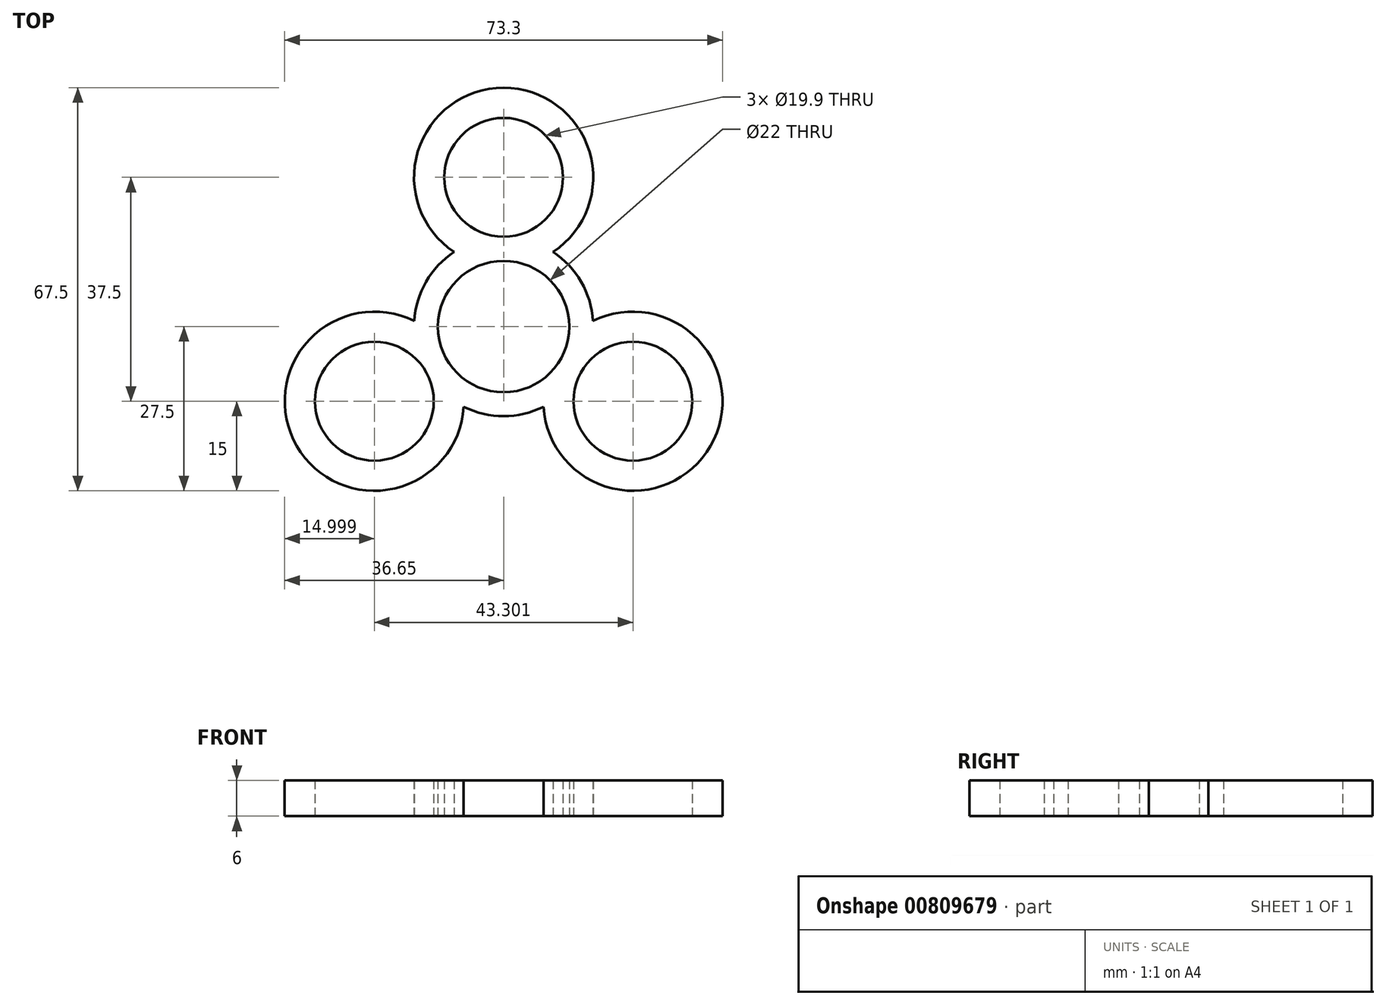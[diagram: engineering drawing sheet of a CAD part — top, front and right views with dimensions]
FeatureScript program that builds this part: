
annotation { "Feature Type Name" : "Feature", "Feature Type Description" : "" }
export const myFeature = defineFeature(function(context is Context, id is Id, definition is map)
    precondition{}
    {
        {
            var Q0;
            Q0=qCreatedBy(makeId("Top.planeOp"),FACE);
            var sketch = newSketch(context, id + "F0", { "sketchPlane" : qUnion([Q0])});
            skArc(sketch, "E0", {"start": v(9.53, 5.5) * mm, "mid": v(0, 11) * mm, "end": v(-9.53, 5.5) * mm});
            skLineSegment(sketch, "E1", {"start": v(0, 0) * mm, "end": v(0, 25) * mm});
            skCircle(sketch, "E2", {"center": v(0, 25) * mm, "radius": 9.95 * mm});
            skArc(sketch, "E3", {"start": v(13, 7.5) * mm, "mid": v(10.93, 10.27) * mm, "end": v(8.3, 12.5) * mm});
            skArc(sketch, "E4", {"start": v(8.3, 12.5) * mm, "mid": v(0, 40) * mm, "end": v(-8.3, 12.5) * mm});
            skArc(sketch, "E5.trimOffspring", {"start": v(-8.3, 12.5) * mm, "mid": v(-10.93, 10.27) * mm, "end": v(-13, 7.5) * mm});
            skArc(sketch, "E6.1.0", {"start": v(-13, 7.5) * mm, "mid": v(-14.36, 4.33) * mm, "end": v(-14.97, 0.93) * mm});
            skArc(sketch, "E6.1.1", {"start": v(-14.97, 0.93) * mm, "mid": v(-34.64, -20) * mm, "end": v(-6.68, -13.43) * mm});
            skCircle(sketch, "E6.1.2", {"center": v(-21.65, -12.5) * mm, "radius": 9.95 * mm});
            skArc(sketch, "E6.1.3", {"start": v(-6.68, -13.43) * mm, "mid": v(-3.43, -14.6) * mm, "end": v(0, -15) * mm});
            skArc(sketch, "E6.1.4", {"start": v(-9.53, 5.5) * mm, "mid": v(-9.53, -5.5) * mm, "end": v(0, -11) * mm});
            skArc(sketch, "E6.2.0", {"start": v(0, -15) * mm, "mid": v(3.43, -14.6) * mm, "end": v(6.68, -13.43) * mm});
            skArc(sketch, "E6.2.1", {"start": v(6.68, -13.43) * mm, "mid": v(34.64, -20) * mm, "end": v(14.97, 0.93) * mm});
            skCircle(sketch, "E6.2.2", {"center": v(21.65, -12.5) * mm, "radius": 9.95 * mm});
            skArc(sketch, "E6.2.3", {"start": v(14.97, 0.93) * mm, "mid": v(14.36, 4.33) * mm, "end": v(13, 7.5) * mm});
            skArc(sketch, "E6.2.4", {"start": v(0, -11) * mm, "mid": v(9.53, -5.5) * mm, "end": v(9.53, 5.5) * mm});
            skSolve(sketch);
        }
        {
            var Q0;
            Q0 = qSketchRegion(id + "F0", true);
            extrude(context, id + "F1", {"entities" : qUnion([Q0]), "depth" : 6 * mm, "offsetDistance" : 25 * mm});
        }
    });
